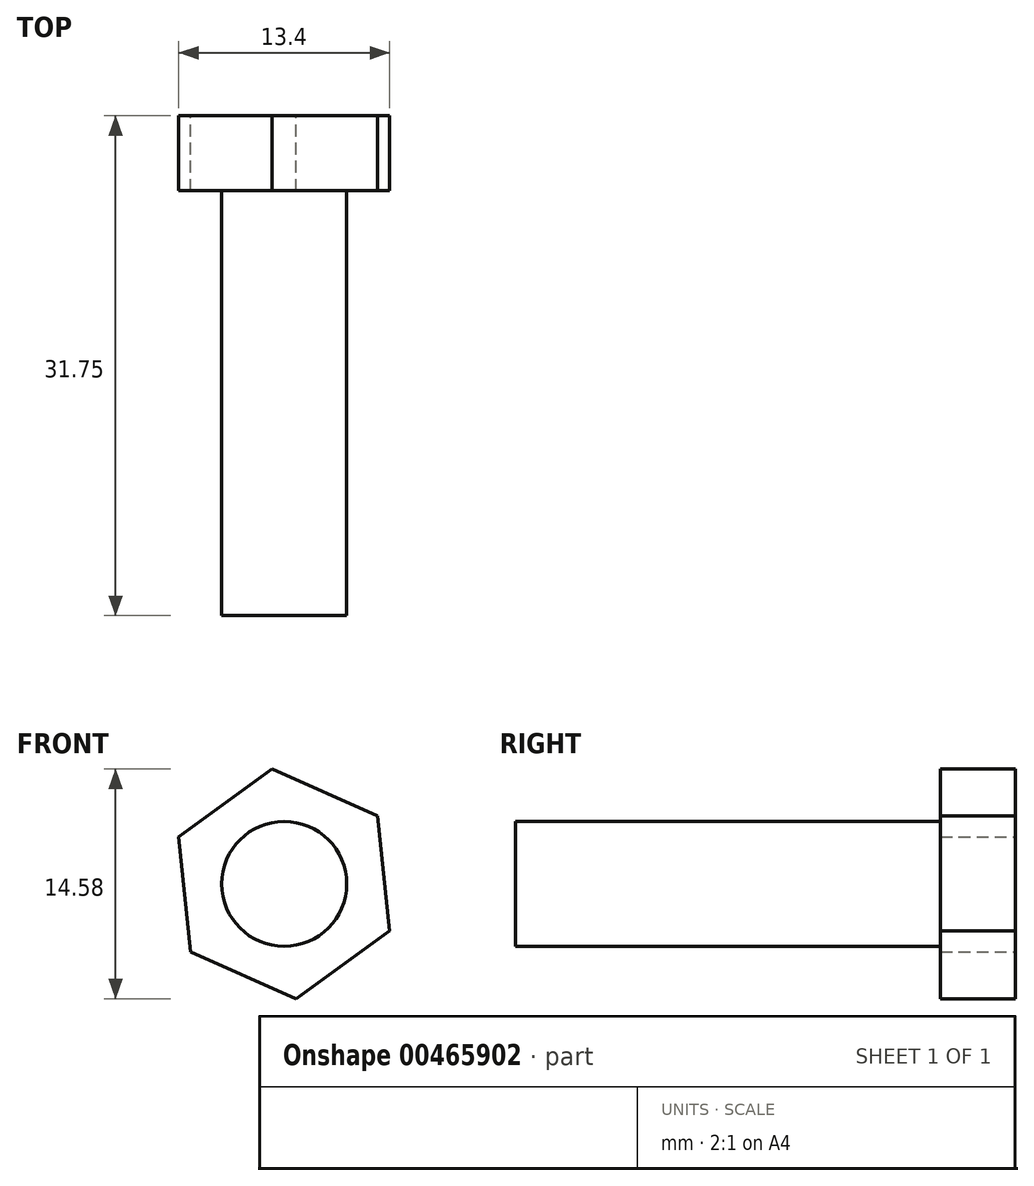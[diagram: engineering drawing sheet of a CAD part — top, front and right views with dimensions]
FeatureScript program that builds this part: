
annotation { "Feature Type Name" : "Feature", "Feature Type Description" : "" }
export const myFeature = defineFeature(function(context is Context, id is Id, definition is map)
    precondition{}
    {
        {
            var Q0;
            Q0=qCreatedBy(makeId("Front.planeOp"),FACE);
            var sketch = newSketch(context, id + "F0", { "sketchPlane" : qUnion([Q0])});
            skCircle(sketch, "E0", {"center": v(0, 0) * mm, "radius": 3.97 * mm});
            skSolve(sketch);
        }
        {
            var Q0;
            Q0=makeQuery(id+"F0.imprint","IMPRINT",FACE,{"disambiguationData":[TD([[makeQuery(id+"F0.imprint","IMPRINT",EDGE,{"derivedFrom":sQuery(id+"F0.wireOp",EDGE,"E0")}),1.0]])]});
            extrude(context, id + "F1", {"entities" : qUnion([Q0]), "depth" : 31.75 * mm});
        }
        {
            var Q0;
            Q0=qCreatedBy(makeId("Front.planeOp"),FACE);
            var sketch = newSketch(context, id + "F2", { "sketchPlane" : qUnion([Q0])});
            skCircle(sketch, "E1", {"center": v(0, 0) * mm, "radius": 6.35 * mm});
            skCircle(sketch, "E2.cCircle", {"center": v(0, 0) * mm, "radius": 6.35 * mm, "construction": true});
            skLineSegment(sketch, "E2.0", {"start": v(-6.7, 2.98) * mm, "end": v(-0.76, 7.3) * mm});
            skLineSegment(sketch, "E2.1", {"start": v(-0.76, 7.3) * mm, "end": v(5.93, 4.3) * mm});
            skLineSegment(sketch, "E2.2", {"start": v(5.93, 4.3) * mm, "end": v(6.7, -2.98) * mm});
            skLineSegment(sketch, "E2.3", {"start": v(6.7, -2.98) * mm, "end": v(0.76, -7.3) * mm});
            skLineSegment(sketch, "E2.4", {"start": v(0.76, -7.3) * mm, "end": v(-5.93, -4.3) * mm});
            skLineSegment(sketch, "E2.5", {"start": v(-5.93, -4.3) * mm, "end": v(-6.7, 2.98) * mm});
            skPoint(sketch, "E2.0.midPoint", {"position": v(-3.73, 5.14) * mm});
            skSolve(sketch);
        }
        {
            var Q0;
            {var subQ0=sQuery(id+"F2.wireOp",EDGE,"E2.5");var subQ1=sQuery(id+"F2.wireOp",EDGE,"E1");var subQ2=makeQuery(id+"F2.imprint","INTERSECT",VERTEX,{"derivedFrom":[subQ1,subQ0]});Q0=makeQuery(id+"F2.imprint","IMPRINT",FACE,{"disambiguationData":[TD([[makeQuery(id+"F2.imprint","IMPRINT",EDGE,{"disambiguationData":[TD([[subQ2,-1.0]])],"derivedFrom":subQ1}),-1.0]])]});}
            var Q1;
            {var subQ0=sQuery(id+"F2.wireOp",EDGE,"E2.0");var subQ1=sQuery(id+"F2.wireOp",EDGE,"E1");var subQ2=makeQuery(id+"F2.imprint","INTERSECT",VERTEX,{"derivedFrom":[subQ1,subQ0]});Q1=makeQuery(id+"F2.imprint","IMPRINT",FACE,{"disambiguationData":[TD([[makeQuery(id+"F2.imprint","IMPRINT",EDGE,{"disambiguationData":[TD([[subQ2,-1.0]])],"derivedFrom":subQ1}),-1.0]])]});}
            var Q2;
            {var subQ0=sQuery(id+"F2.wireOp",EDGE,"E2.4");var subQ1=sQuery(id+"F2.wireOp",EDGE,"E1");var subQ2=makeQuery(id+"F2.imprint","INTERSECT",VERTEX,{"derivedFrom":[subQ1,subQ0]});Q2=makeQuery(id+"F2.imprint","IMPRINT",FACE,{"disambiguationData":[TD([[makeQuery(id+"F2.imprint","IMPRINT",EDGE,{"disambiguationData":[TD([[subQ2,-1.0]])],"derivedFrom":subQ1}),-1.0]])]});}
            var Q3;
            {var subQ0=sQuery(id+"F2.wireOp",EDGE,"E2.2");var subQ1=sQuery(id+"F2.wireOp",EDGE,"E1");var subQ2=makeQuery(id+"F2.imprint","INTERSECT",VERTEX,{"derivedFrom":[subQ1,subQ0]});Q3=makeQuery(id+"F2.imprint","IMPRINT",FACE,{"disambiguationData":[TD([[makeQuery(id+"F2.imprint","IMPRINT",EDGE,{"disambiguationData":[TD([[subQ2,1.0]])],"derivedFrom":subQ1}),-1.0]])]});}
            var Q4;
            {var subQ0=sQuery(id+"F2.wireOp",EDGE,"E2.1");var subQ1=sQuery(id+"F2.wireOp",EDGE,"E1");var subQ2=makeQuery(id+"F2.imprint","INTERSECT",VERTEX,{"derivedFrom":[subQ1,subQ0]});Q4=makeQuery(id+"F2.imprint","IMPRINT",FACE,{"disambiguationData":[TD([[makeQuery(id+"F2.imprint","IMPRINT",EDGE,{"disambiguationData":[TD([[subQ2,1.0]])],"derivedFrom":subQ1}),-1.0]])]});}
            var Q5;
            {var subQ0=sQuery(id+"F2.wireOp",EDGE,"E2.1");var subQ1=sQuery(id+"F2.wireOp",EDGE,"E1");var subQ2=makeQuery(id+"F2.imprint","INTERSECT",VERTEX,{"derivedFrom":[subQ1,subQ0]});Q5=makeQuery(id+"F2.imprint","IMPRINT",FACE,{"disambiguationData":[TD([[makeQuery(id+"F2.imprint","IMPRINT",EDGE,{"disambiguationData":[TD([[subQ2,-1.0]])],"derivedFrom":subQ1}),-1.0]])]});}
            var Q6;
            {var subQ0=sQuery(id+"F2.wireOp",EDGE,"E1");var subQ4=makeQuery(id+"F2.imprint","INTERSECT",VERTEX,{"derivedFrom":[subQ0,sQuery(id+"F2.wireOp",EDGE,"E2.1")]});Q6=makeQuery(id+"F2.imprint","IMPRINT",FACE,{"disambiguationData":[TD([[makeQuery(id+"F2.imprint","IMPRINT",EDGE,{"disambiguationData":[TD([[subQ4,1.0]])],"derivedFrom":subQ0}),1.0]])]});}
            extrude(context, id + "F3", {"entities" : qUnion([Q0, Q1, Q2, Q3, Q4, Q5, Q6]), "operationType" : NewBodyOperationType.ADD, "depth" : 4.76 * mm});
        }
    });
